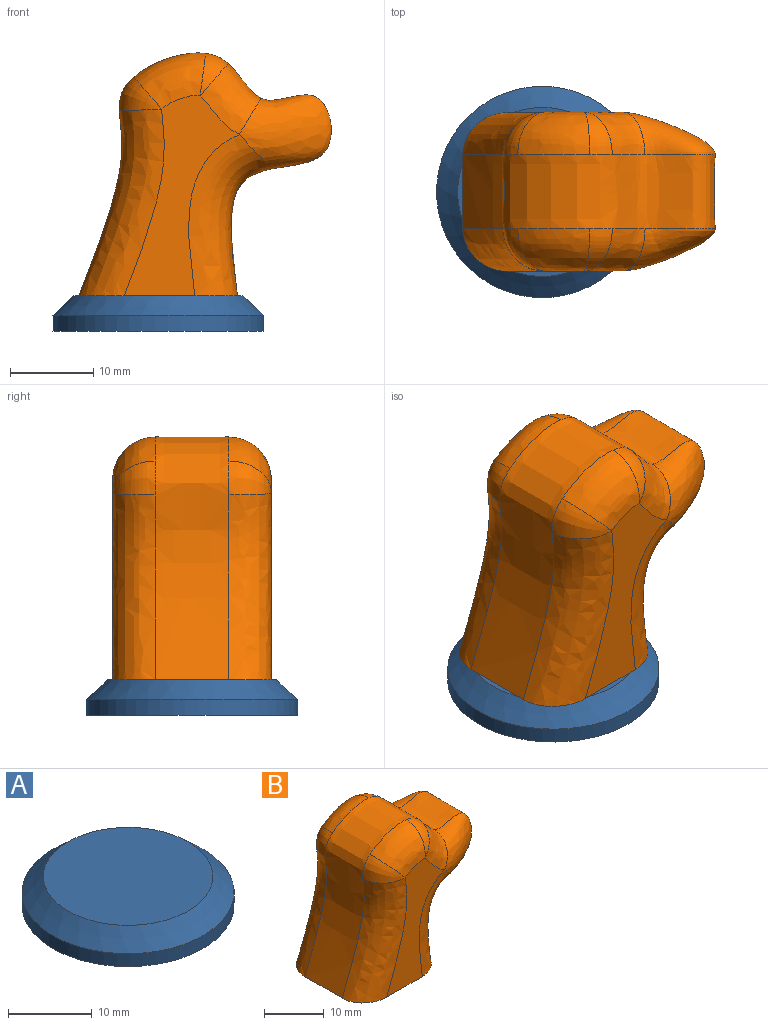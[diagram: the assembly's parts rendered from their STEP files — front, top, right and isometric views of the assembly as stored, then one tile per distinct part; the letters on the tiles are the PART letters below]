
ASSEMBLY  parts=2 mates=1
PART A: 4 faces, bbox 25.4x25.4x4.2 mm
  f0: plane 20.32x20.32mm, normal (0,0,1), area 324.3mm2, adj f3
  f1: plane 25.4x25.4mm, normal (0,0,-1), area 506.7mm2, adj f2
  f2: cylinder r=12.7mm len=25.4mm, axis (0,0,1), area 150.7mm2, adj f1,f3
  f3: cone r=12.7mm half-angle=47.1deg, axis (0,0,-1), area 249mm2, adj f0,f2
PART B: 18 faces, bbox 32.1x19.9x34.3 mm
  f0: extruded ~30.33x29.11mm, area 752.3mm2, adj f1,f4,f5,f6,f7,f8,f9,f10
  f1: plane 19.88x19.88mm, normal (0,0,-1), area 339.8mm2, adj f0,f2,f3,f4,f10,f11,f17
  f2: plane 24.11x13.81mm, normal (0,-1,0), area 137.3mm2, adj f1,f11,f13,f15,f17
  f3: plane 24.11x13.81mm, normal (0,1,0), area 137.3mm2, adj f1,f4,f6,f8,f10
  f4: bspline ~23.44x11.03mm, area 151.4mm2, adj f0,f1,f3,f5
  f5: bspline ~11.09x8.9mm, area 106.4mm2, adj f0,f4,f6
  f6: bspline ~9.33x7.58mm, area 48.7mm2, adj f0,f3,f5,f7
  f7: bspline ~5.08x5.04mm, area 9.8mm2, adj f0,f6,f8
  f8: bspline ~9.37x6.86mm, area 62mm2, adj f0,f3,f7,f9
  f9: bspline ~5.1x5.08mm, area 14.7mm2, adj f0,f8,f10
  f10: bspline ~27.04x11.25mm, area 182.3mm2, adj f0,f1,f3,f9
  f11: bspline ~23.48x11.03mm, area 151.4mm2, adj f0,f1,f2,f12
  f12: bspline ~11.09x8.9mm, area 106.1mm2, adj f0,f11,f13
  f13: bspline ~9.32x7.58mm, area 48.9mm2, adj f0,f2,f12,f14
  f14: bspline ~5.08x5.04mm, area 12.6mm2, adj f0,f13,f15
  f15: bspline ~9.13x6.8mm, area 62mm2, adj f0,f2,f14,f16
  f16: bspline ~5.1x5.08mm, area 14.7mm2, adj f0,f15,f17
  f17: bspline ~27.02x11.25mm, area 182.3mm2, adj f0,f1,f2,f16
PLACE A t=(2.27,2.95,0.33)mm
PLACE B t=(-7.27,12.48,4.58)mm
MATE fastened B.f1 <-> A.f2  axis (0,0,-1) through (2.27,2.95,4.58)mm
